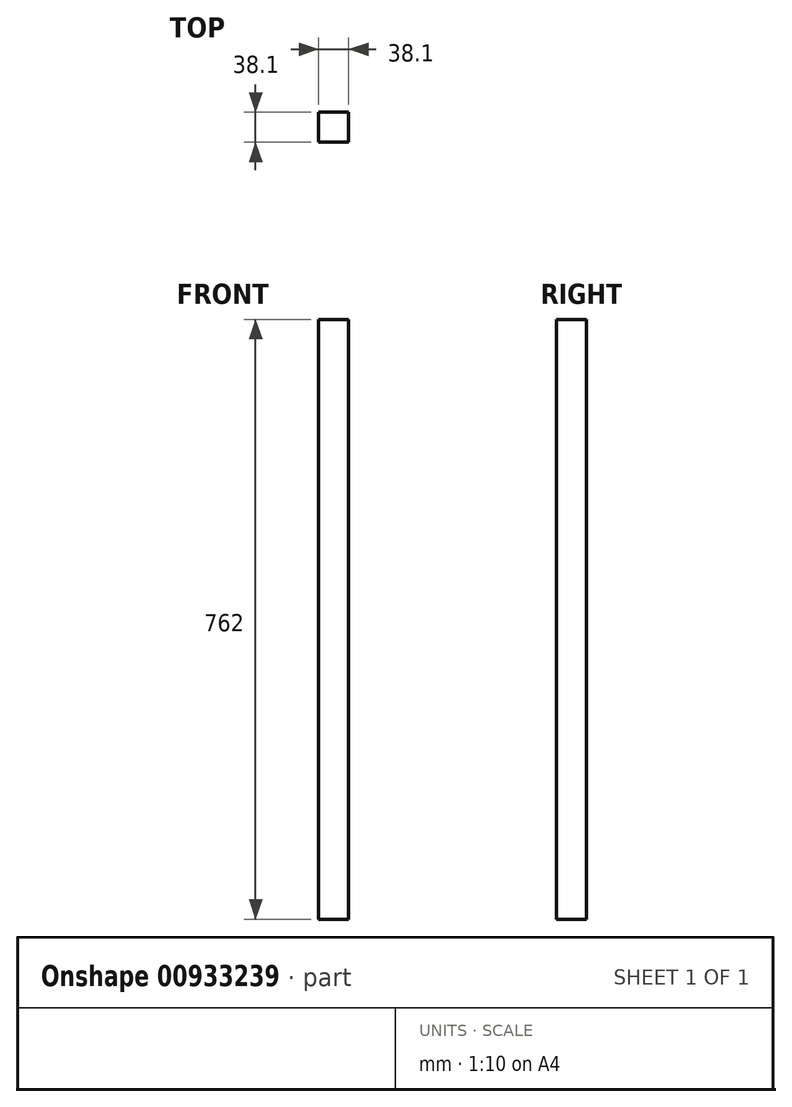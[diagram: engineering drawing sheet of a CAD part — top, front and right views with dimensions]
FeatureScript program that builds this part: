
annotation { "Feature Type Name" : "Feature", "Feature Type Description" : "" }
export const myFeature = defineFeature(function(context is Context, id is Id, definition is map)
    precondition{}
    {
        {
            var Q0;
            Q0=qCreatedBy(makeId("Front.planeOp"),FACE);
            var sketch = newSketch(context, id + "F0", { "sketchPlane" : qUnion([Q0])});
            skLineSegment(sketch, "E0.bottom", {"start": v(-19.05, -381) * mm, "end": v(19.05, -381) * mm});
            skLineSegment(sketch, "E0.top", {"start": v(-19.05, 381) * mm, "end": v(19.05, 381) * mm});
            skLineSegment(sketch, "E0.left", {"start": v(-19.05, -381) * mm, "end": v(-19.05, 381) * mm});
            skLineSegment(sketch, "E0.right", {"start": v(19.05, -381) * mm, "end": v(19.05, 381) * mm});
            skPoint(sketch, "E0.middle", {"position": v(0, 0) * mm});
            skSolve(sketch);
        }
        {
            var Q0;
            Q0=qSketchRegion(id+"F0",true);
            extrude(context, id + "F1", {"entities" : qUnion([Q0]), "depth" : 38.1 * mm, "offsetDistance" : 25.4 * mm});
        }
    });
